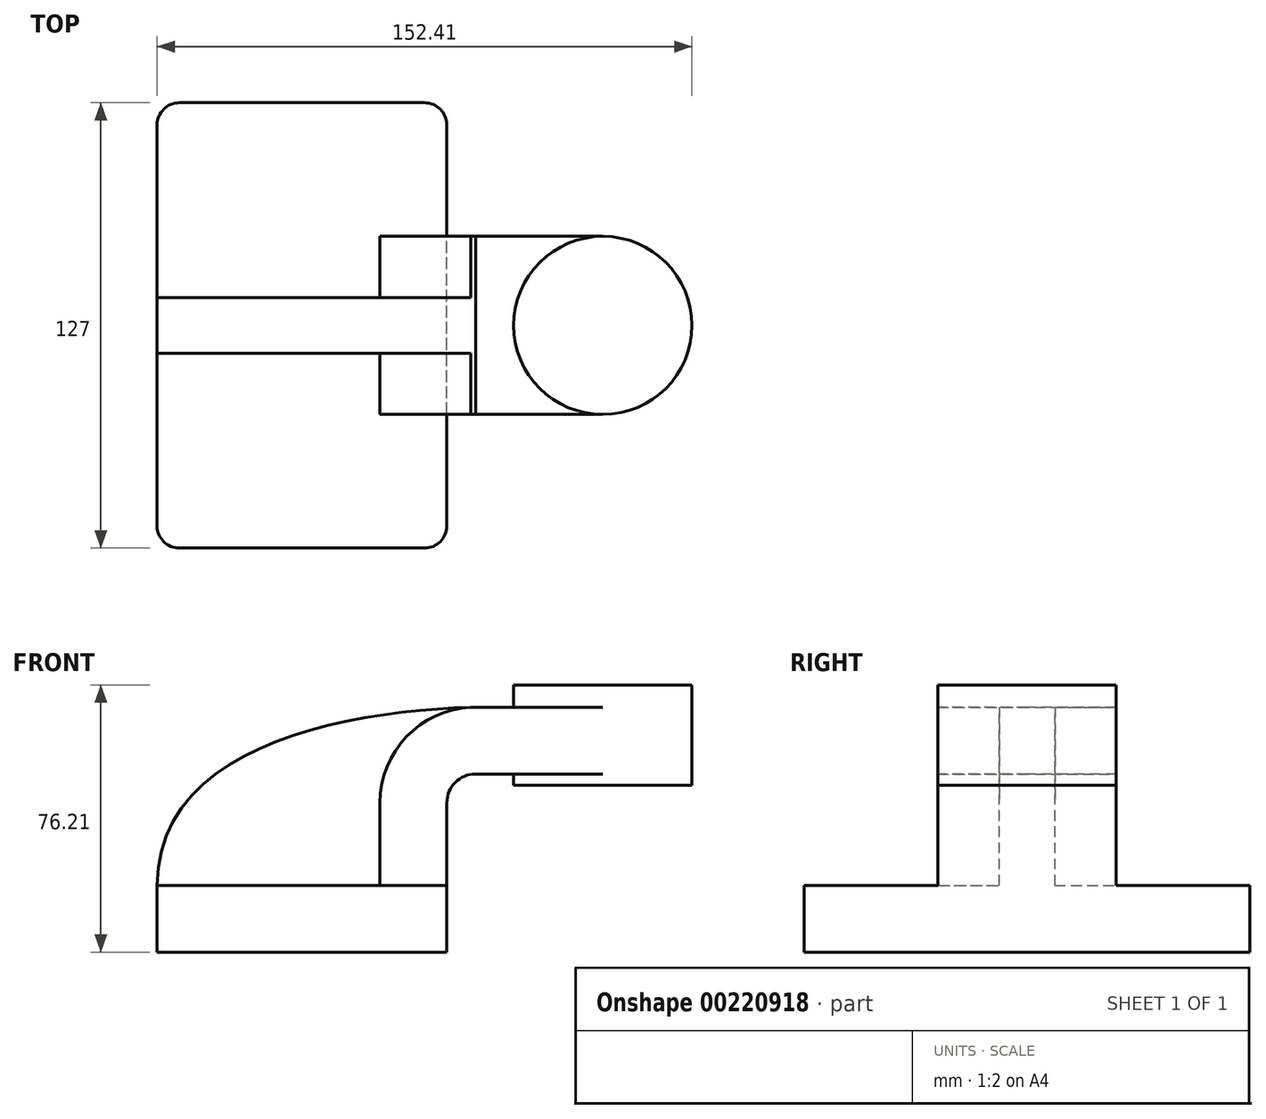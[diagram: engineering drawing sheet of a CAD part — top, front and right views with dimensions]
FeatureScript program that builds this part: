
annotation { "Feature Type Name" : "Feature", "Feature Type Description" : "" }
export const myFeature = defineFeature(function(context is Context, id is Id, definition is map)
    precondition{}
    {
        {
            var Q0;
            Q0=qCreatedBy(makeId("Front.planeOp"),FACE);
            var sketch = newSketch(context, id + "F0", { "sketchPlane" : qUnion([Q0])});
            skLineSegment(sketch, "E0.bottom", {"start": v(41.27, 9.53) * mm, "end": v(-41.28, 9.53) * mm});
            skLineSegment(sketch, "E0.top", {"start": v(41.28, -9.52) * mm, "end": v(-41.27, -9.52) * mm});
            skLineSegment(sketch, "E0.left", {"start": v(41.28, 9.53) * mm, "end": v(41.28, -9.52) * mm});
            skLineSegment(sketch, "E0.right", {"start": v(-41.28, 9.53) * mm, "end": v(-41.27, -9.52) * mm});
            skPoint(sketch, "E0.middle", {"position": v(0, 0) * mm});
            skLineSegment(sketch, "E1.bottom", {"start": v(111.12, 38.1) * mm, "end": v(60.33, 38.1) * mm});
            skLineSegment(sketch, "E1.top", {"start": v(111.12, 66.68) * mm, "end": v(60.33, 66.68) * mm});
            skLineSegment(sketch, "E1.left", {"start": v(111.12, 38.1) * mm, "end": v(111.12, 66.68) * mm});
            skLineSegment(sketch, "E1.right", {"start": v(60.33, 38.1) * mm, "end": v(60.33, 66.68) * mm});
            skPoint(sketch, "E1.middle", {"position": v(85.72, 52.39) * mm});
            skLineSegment(sketch, "E2", {"start": v(41.27, 9.53) * mm, "end": v(41.27, 33.02) * mm});
            skArc(sketch, "E3", {"start": v(41.28, 33.02) * mm, "mid": v(43.7, 38.86) * mm, "end": v(49.53, 41.28) * mm});
            skLineSegment(sketch, "E4", {"start": v(49.53, 41.28) * mm, "end": v(85.72, 41.28) * mm});
            skLineSegment(sketch, "E5.0", {"start": v(49.53, 60.33) * mm, "end": v(85.72, 60.33) * mm});
            skArc(sketch, "E5.1", {"start": v(22.23, 33.02) * mm, "mid": v(30.22, 52.33) * mm, "end": v(49.53, 60.33) * mm});
            skLineSegment(sketch, "E5.2", {"start": v(22.22, 9.53) * mm, "end": v(22.22, 33.02) * mm});
            skLineSegment(sketch, "E6", {"start": v(85.72, 38.1) * mm, "end": v(85.72, 66.68) * mm});
            skFitSpline(sketch, "E7", {"points": [v(-41.28, 9.52) * mm, v(49.53, 60.33) * mm], "startDerivative": vector(0.03, 121.57) * mm, "endDerivative": vector(105.1, 2.39) * mm});
            skSolve(sketch);
        }
        {
            var Q0;
            Q0=makeQuery(id+"F0.imprint","IMPRINT",FACE,{"disambiguationData":[TD([[makeQuery(id+"F0.imprint","IMPRINT",EDGE,{"derivedFrom":sQuery(id+"F0.wireOp",EDGE,"E0.top")}),-1.0]])]});
            extrude(context, id + "F1", {"entities" : qUnion([Q0]), "endBound" : BoundingType.SYMMETRIC, "depth" : 127 * mm});
        }
        {
            var Q0;
            {var subQ1=sQuery(id+"F0.wireOp",EDGE,"E2");Q0=makeQuery(id+"F0.imprint","IMPRINT",FACE,{"disambiguationData":[TD([[makeQuery(id+"F0.imprint","IMPRINT",EDGE,{"derivedFrom":subQ1}),1.0]])]});}
            var Q1;
            {var subQ0=sQuery(id+"F0.wireOp",EDGE,"E4");var subQ1=sQuery(id+"F0.wireOp",EDGE,"E1.right");var subQ2=makeQuery(id+"F0.imprint","INTERSECT",VERTEX,{"derivedFrom":[subQ1,subQ0]});Q1=makeQuery(id+"F0.imprint","IMPRINT",FACE,{"disambiguationData":[TD([[makeQuery(id+"F0.imprint","IMPRINT",EDGE,{"disambiguationData":[TD([[subQ2,-1.0]])],"derivedFrom":subQ1}),-1.0]])]});}
            extrude(context, id + "F2", {"entities" : qUnion([Q0, Q1]), "operationType" : NewBodyOperationType.ADD, "endBound" : BoundingType.SYMMETRIC, "depth" : 50.8 * mm});
        }
        {
            var Q0;
            {var subQ3=sQuery(id+"F0.wireOp",EDGE,"E5.2");Q0=makeQuery(id+"F0.imprint","IMPRINT",FACE,{"disambiguationData":[TD([[makeQuery(id+"F0.imprint","IMPRINT",EDGE,{"derivedFrom":subQ3}),1.0]])]});}
            extrude(context, id + "F3", {"entities" : qUnion([Q0]), "operationType" : NewBodyOperationType.ADD, "endBound" : BoundingType.SYMMETRIC, "depth" : 15.88 * mm});
        }
        {
            var Q0;
            Q0=makeQuery(id+"F1.opExtrude","CAP_EDGE",EDGE,{"disambiguationData":[OSD([sQuery(id+"F0.wireOp",EDGE,"E0.left")])],"isStart":false});
            var Q1;
            Q1=makeQuery(id+"F1.opExtrude","CAP_EDGE",EDGE,{"disambiguationData":[OSD([sQuery(id+"F0.wireOp",EDGE,"E0.right")])],"isStart":false});
            var Q2;
            Q2=makeQuery(id+"F1.opExtrude","CAP_EDGE",EDGE,{"disambiguationData":[OSD([sQuery(id+"F0.wireOp",EDGE,"E0.left")])],"isStart":true});
            var Q3;
            Q3=makeQuery(id+"F1.opExtrude","CAP_EDGE",EDGE,{"disambiguationData":[OSD([sQuery(id+"F0.wireOp",EDGE,"E0.right")])],"isStart":true});
            fillet(context, id + "F4", {"entities" : qUnion([Q0, Q1, Q2, Q3]), "radius" : 6.35 * mm, "tangentPropagation" : true, "allowEdgeOverflow" : false});
        }
        {
            var Q0;
            {var subQ0=sQuery(id+"F0.wireOp",EDGE,"E1.left");Q0=makeQuery(id+"F0.imprint","IMPRINT",FACE,{"disambiguationData":[TD([[makeQuery(id+"F0.imprint","IMPRINT",EDGE,{"derivedFrom":subQ0}),1.0]])]});}
            var Q1;
            Q1=sQuery(id+"F0.wireOp",EDGE,"E6");
            revolve(context, id + "F5", {"operationType" : NewBodyOperationType.ADD, "entities" : qUnion([Q0]), "axis" : qUnion([Q1]), "revolveType" : RevolveType.FULL});
        }
    });
